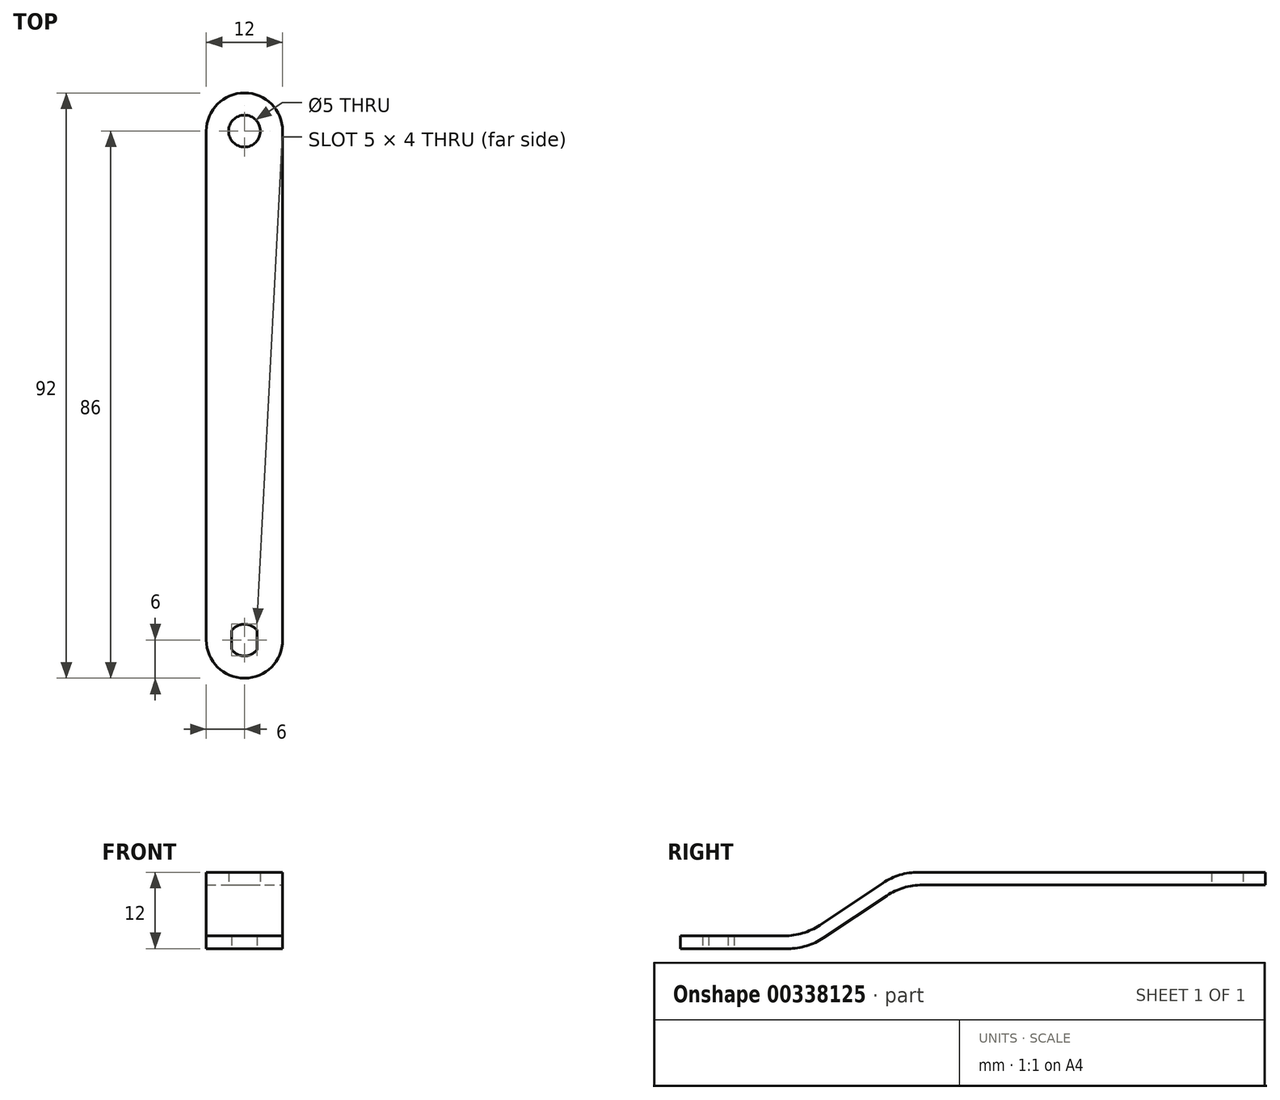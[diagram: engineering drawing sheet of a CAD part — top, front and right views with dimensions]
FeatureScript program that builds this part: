
annotation { "Feature Type Name" : "Feature", "Feature Type Description" : "" }
export const myFeature = defineFeature(function(context is Context, id is Id, definition is map)
    precondition{}
    {
        {
            var Q0;
            Q0=qCreatedBy(makeId("Right.planeOp"),FACE);
            var sketch = newSketch(context, id + "F0", { "sketchPlane" : qUnion([Q0])});
            skLineSegment(sketch, "E0", {"start": v(0, 0) * mm, "end": v(20, 0) * mm});
            skLineSegment(sketch, "E1", {"start": v(20, 0) * mm, "end": v(35, 10) * mm});
            skLineSegment(sketch, "E2", {"start": v(35, 10) * mm, "end": v(92, 10) * mm});
            skSolve(sketch);
        }
        {
            var Q0;
            Q0=qCreatedBy(makeId("Front.planeOp"),FACE);
            var sketch = newSketch(context, id + "F1", { "sketchPlane" : qUnion([Q0])});
            skLineSegment(sketch, "E3.bottom", {"start": v(-6, 2) * mm, "end": v(6, 2) * mm});
            skLineSegment(sketch, "E3.top", {"start": v(-6, 0) * mm, "end": v(6, 0) * mm});
            skLineSegment(sketch, "E3.left", {"start": v(-6, 2) * mm, "end": v(-6, 0) * mm});
            skLineSegment(sketch, "E3.right", {"start": v(6, 2) * mm, "end": v(6, 0) * mm});
            skSolve(sketch);
        }
        {
            var Q0;
            Q0 = qSketchRegion(id + "F1", true);
            var Q1;
            Q1 = qConstructionFilter(qBodyType(qCreatedBy(id + "F0" ,EDGE), BodyType.WIRE), ConstructionObject.NO);
            sweep(context, id + "F2", {"profiles" : qUnion([Q0]), "path" : qUnion([Q1])});
        }
        {
            var Q0;
            Q0=makeQuery(id+"F2.opSweep","MID_CAP_EDGE",EDGE,{"disambiguationData":[OSD([sQuery(id+"F0.wireOp",VERTEX,"E1.start"),sQuery(id+"F1.wireOp",EDGE,"E3.bottom")])],"capPos":1.0});
            var Q1;
            Q1=makeQuery(id+"F2.opSweep","MID_CAP_EDGE",EDGE,{"disambiguationData":[OSD([sQuery(id+"F0.wireOp",VERTEX,"E2.start"),sQuery(id+"F1.wireOp",EDGE,"E3.bottom")])],"capPos":2.0});
            var Q2;
            Q2=makeQuery(id+"F2.opSweep","MID_CAP_EDGE",EDGE,{"disambiguationData":[OSD([sQuery(id+"F0.wireOp",VERTEX,"E2.start"),sQuery(id+"F1.wireOp",EDGE,"E3.top")])],"capPos":2.0});
            var Q3;
            Q3=makeQuery(id+"F2.opSweep","MID_CAP_EDGE",EDGE,{"disambiguationData":[OSD([sQuery(id+"F0.wireOp",VERTEX,"E1.start"),sQuery(id+"F1.wireOp",EDGE,"E3.top")])],"capPos":1.0});
            fillet(context, id + "F3", {"entities" : qUnion([Q0, Q1, Q2, Q3]), "radius" : 10 * mm, "tangentPropagation" : true, "allowEdgeOverflow" : false});
        }
        {
            var Q0;
            Q0=qCreatedBy(makeId("Top.planeOp"),FACE);
            var sketch = newSketch(context, id + "F4", { "sketchPlane" : qUnion([Q0])});
            skArc(sketch, "E4", {"start": v(2, 7.5) * mm, "mid": v(0, 8.5) * mm, "end": v(-2, 7.5) * mm});
            skLineSegment(sketch, "E5", {"start": v(-2, 7.5) * mm, "end": v(-2, 4.5) * mm});
            skLineSegment(sketch, "E6", {"start": v(2, 7.5) * mm, "end": v(2, 4.5) * mm});
            skArc(sketch, "E7.trimOffspring", {"start": v(-2, 4.5) * mm, "mid": v(0, 3.5) * mm, "end": v(2, 4.5) * mm});
            skSolve(sketch);
        }
        {
            var Q0;
            Q0 = qSketchRegion(id + "F4", true);
            extrude(context, id + "F5", {"entities" : qUnion([Q0]), "operationType" : NewBodyOperationType.REMOVE, "endBound" : BoundingType.THROUGH_ALL, "depth" : 25 * mm});
        }
        {
            var Q0;
            Q0=qCreatedBy(makeId("Top.planeOp"),FACE);
            var sketch = newSketch(context, id + "F6", { "sketchPlane" : qUnion([Q0])});
            skCircle(sketch, "E8", {"center": v(0, 86) * mm, "radius": 2.5 * mm});
            skSolve(sketch);
        }
        {
            var Q0;
            Q0 = qSketchRegion(id + "F6", true);
            extrude(context, id + "F7", {"entities" : qUnion([Q0]), "operationType" : NewBodyOperationType.REMOVE, "endBound" : BoundingType.THROUGH_ALL, "depth" : 25 * mm});
        }
        {
            var Q0;
            Q0=makeQuery(id+"F2.opSweep","CAP_EDGE",EDGE,{"disambiguationData":[OSD([sQuery(id+"F0.wireOp",VERTEX,"E0.start"),sQuery(id+"F1.wireOp",EDGE,"E3.left")])],"isStart":true});
            var Q1;
            Q1=makeQuery(id+"F2.opSweep","CAP_EDGE",EDGE,{"disambiguationData":[OSD([sQuery(id+"F0.wireOp",VERTEX,"E0.start"),sQuery(id+"F1.wireOp",EDGE,"E3.right")])],"isStart":true});
            fillet(context, id + "F8", {"entities" : qUnion([Q0, Q1]), "radius" : 6 * mm, "tangentPropagation" : true, "allowEdgeOverflow" : false});
        }
        {
            var Q0;
            Q0=makeQuery(id+"F2.opSweep","CAP_EDGE",EDGE,{"disambiguationData":[OSD([sQuery(id+"F0.wireOp",VERTEX,"E2.end"),sQuery(id+"F1.wireOp",EDGE,"E3.right")])],"isStart":false});
            var Q1;
            Q1=makeQuery(id+"F2.opSweep","CAP_EDGE",EDGE,{"disambiguationData":[OSD([sQuery(id+"F0.wireOp",VERTEX,"E2.end"),sQuery(id+"F1.wireOp",EDGE,"E3.left")])],"isStart":false});
            fillet(context, id + "F9", {"entities" : qUnion([Q0, Q1]), "radius" : 6 * mm, "tangentPropagation" : true, "allowEdgeOverflow" : false});
        }
    });
